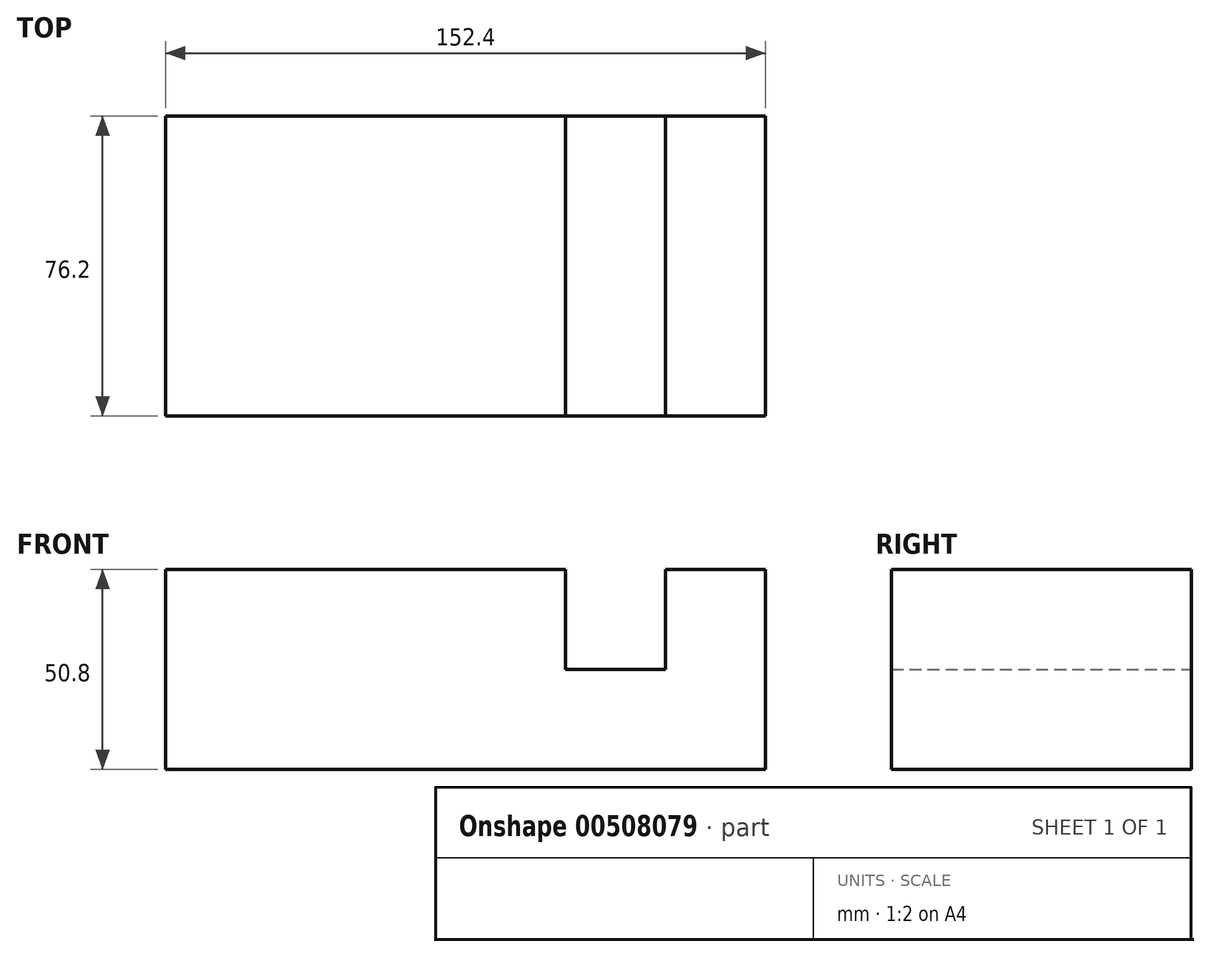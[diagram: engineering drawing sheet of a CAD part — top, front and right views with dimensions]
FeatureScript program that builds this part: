
annotation { "Feature Type Name" : "Feature", "Feature Type Description" : "" }
export const myFeature = defineFeature(function(context is Context, id is Id, definition is map)
    precondition{}
    {
        {
            var Q0;
            Q0=qCreatedBy(makeId("Front.planeOp"),FACE);
            var sketch = newSketch(context, id + "F0", { "sketchPlane" : qUnion([Q0])});
            skLineSegment(sketch, "E0", {"start": v(-133.97, 1.36) * mm, "end": v(-32.37, 1.36) * mm});
            skLineSegment(sketch, "E1", {"start": v(-32.37, 1.36) * mm, "end": v(-32.37, -24.04) * mm});
            skLineSegment(sketch, "E2", {"start": v(-32.37, -24.04) * mm, "end": v(-6.97, -24.04) * mm});
            skLineSegment(sketch, "E3", {"start": v(-6.97, -24.04) * mm, "end": v(-6.97, 1.36) * mm});
            skLineSegment(sketch, "E4", {"start": v(-6.97, 1.36) * mm, "end": v(18.43, 1.36) * mm});
            skLineSegment(sketch, "E5", {"start": v(18.43, 1.36) * mm, "end": v(18.43, -49.44) * mm});
            skLineSegment(sketch, "E6", {"start": v(18.43, -49.44) * mm, "end": v(-133.97, -49.44) * mm});
            skLineSegment(sketch, "E7", {"start": v(-133.97, -49.44) * mm, "end": v(-133.97, 1.36) * mm});
            skSolve(sketch);
        }
        {
            var Q0;
            Q0=makeQuery(id+"F0.imprint","IMPRINT",FACE,{"disambiguationData":[TD([[makeQuery(id+"F0.imprint","IMPRINT",EDGE,{"derivedFrom":sQuery(id+"F0.wireOp",EDGE,"E0")}),-1.0]])]});
            extrude(context, id + "F1", {"entities" : qUnion([Q0]), "depth" : 76.2 * mm});
        }
    });
